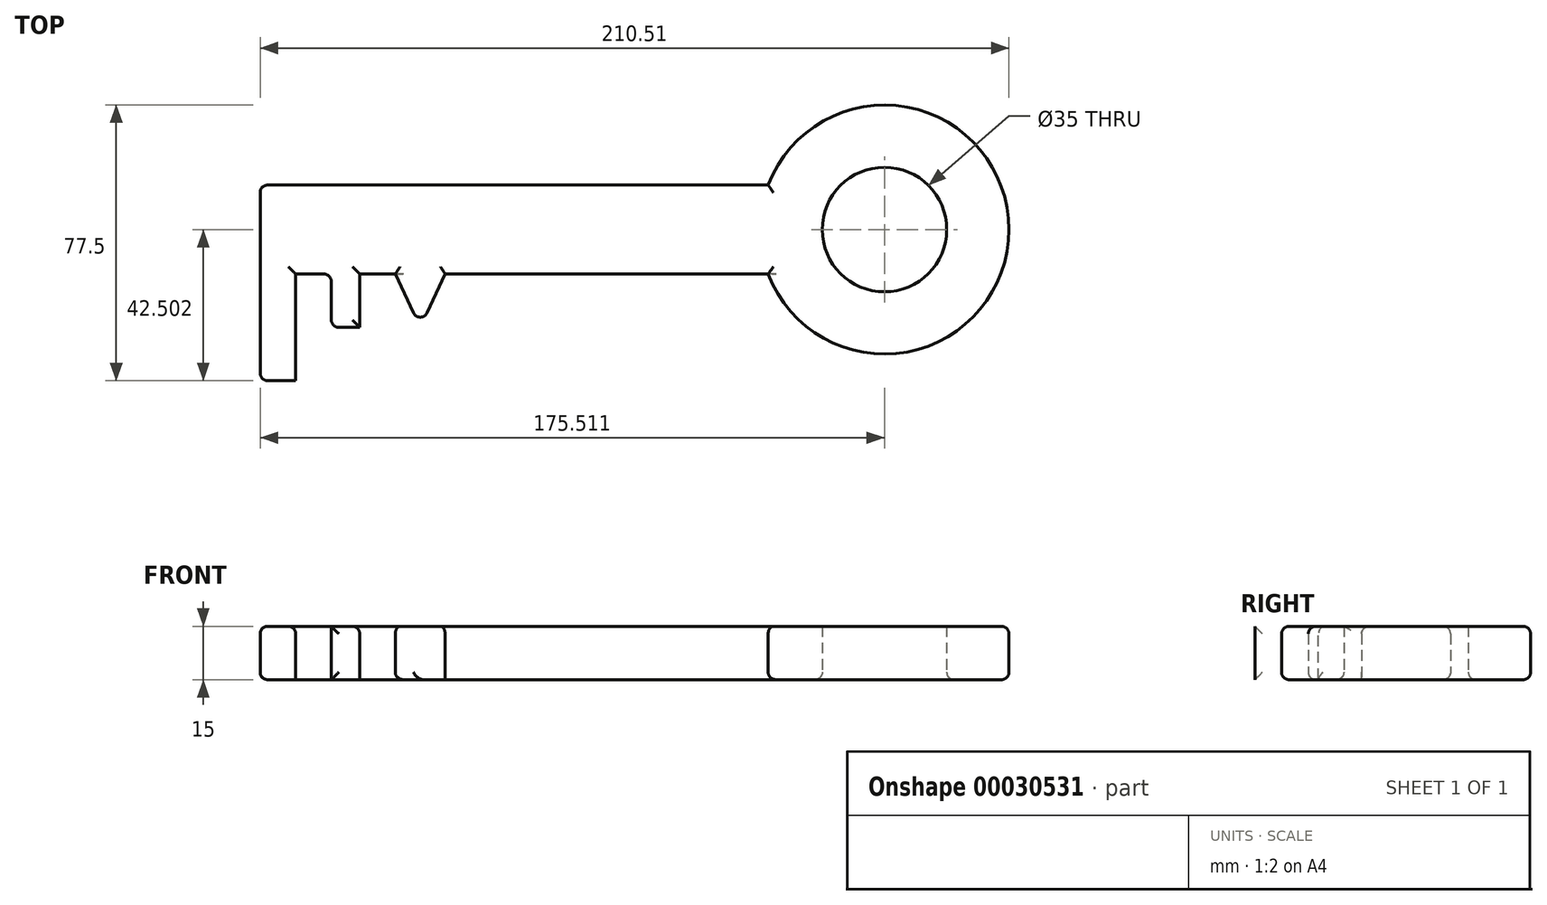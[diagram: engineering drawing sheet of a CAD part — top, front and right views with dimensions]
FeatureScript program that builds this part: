
annotation { "Feature Type Name" : "Feature", "Feature Type Description" : "" }
export const myFeature = defineFeature(function(context is Context, id is Id, definition is map)
    precondition{}
    {
        {
            var Q0;
            Q0=qCreatedBy(makeId("Top.planeOp"),FACE);
            var sketch = newSketch(context, id + "F0", { "sketchPlane" : qUnion([Q0])});
            skLineSegment(sketch, "E0.bottom", {"start": v(-113.6, 29.5) * mm, "end": v(29.23, 29.5) * mm});
            skLineSegment(sketch, "E0.top", {"start": v(-113.6, 4.5) * mm, "end": v(29.23, 4.5) * mm});
            skLineSegment(sketch, "E0.left", {"start": v(-113.6, 29.5) * mm, "end": v(-113.6, 4.5) * mm});
            skLineSegment(sketch, "E0.right", {"start": v(29.23, 29.5) * mm, "end": v(29.23, 4.5) * mm});
            skLineSegment(sketch, "E1.bottom", {"start": v(-113.6, 4.5) * mm, "end": v(-103.6, 4.5) * mm});
            skLineSegment(sketch, "E1.top", {"start": v(-113.6, -25.5) * mm, "end": v(-103.6, -25.5) * mm});
            skLineSegment(sketch, "E1.left", {"start": v(-113.6, 4.5) * mm, "end": v(-113.6, -25.5) * mm});
            skLineSegment(sketch, "E1.right", {"start": v(-103.6, 4.5) * mm, "end": v(-103.6, -25.5) * mm});
            skLineSegment(sketch, "E2.bottom", {"start": v(-93.6, 4.5) * mm, "end": v(-85.6, 4.5) * mm});
            skLineSegment(sketch, "E2.top", {"start": v(-93.6, -10.5) * mm, "end": v(-85.6, -10.5) * mm});
            skLineSegment(sketch, "E2.left", {"start": v(-93.6, 4.5) * mm, "end": v(-93.6, -10.5) * mm});
            skLineSegment(sketch, "E2.right", {"start": v(-85.6, 4.5) * mm, "end": v(-85.6, -10.5) * mm});
            skLineSegment(sketch, "E3", {"start": v(-75.6, 4.5) * mm, "end": v(-68.6, -10.5) * mm});
            skArc(sketch, "E4", {"start": v(29.23, 4.5) * mm, "mid": v(96.92, 17) * mm, "end": v(29.23, 29.5) * mm});
            skCircle(sketch, "E5", {"center": v(61.92, 17) * mm, "radius": 17.5 * mm});
            skLineSegment(sketch, "E6", {"start": v(-61.6, 4.5) * mm, "end": v(-68.6, -10.5) * mm});
            skSolve(sketch);
        }
        {
            var Q0;
            Q0 = qSketchRegion(id + "F0", true);
            extrude(context, id + "F1", {"entities" : qUnion([Q0]), "depth" : 15 * mm});
        }
        {
            var Q0;
            Q0=makeQuery(id+"F1.opExtrude","CAP_EDGE",EDGE,{"disambiguationData":[OSD([sQuery(id+"F0.wireOp",EDGE,"E0.left"),sQuery(id+"F0.wireOp",EDGE,"E1.left")])],"isStart":true});
            var Q1;
            Q1=makeQuery(id+"F1.opExtrude","SWEPT_EDGE",EDGE,{"disambiguationData":[OSD([sQuery(id+"F0.wireOp",EDGE,"E0.bottom"),sQuery(id+"F0.wireOp",EDGE,"E0.left")])]});
            var Q2;
            Q2=makeQuery(id+"F1.opExtrude","CAP_EDGE",EDGE,{"disambiguationData":[OSD([sQuery(id+"F0.wireOp",EDGE,"E0.left"),sQuery(id+"F0.wireOp",EDGE,"E1.left")])],"isStart":false});
            var Q3;
            Q3=makeQuery(id+"F1.opExtrude","SWEPT_EDGE",EDGE,{"disambiguationData":[OSD([sQuery(id+"F0.wireOp",EDGE,"E1.top"),sQuery(id+"F0.wireOp",EDGE,"E1.left")])]});
            var Q4;
            Q4=makeQuery(id+"F1.opExtrude","CAP_EDGE",EDGE,{"disambiguationData":[OSD([sQuery(id+"F0.wireOp",EDGE,"E0.bottom")])],"isStart":true});
            var Q5;
            {var subQ0=sQuery(id+"F0.wireOp",EDGE,"E0.top");Q5=makeQuery(id+"F1.opExtrude","CAP_EDGE",EDGE,{"disambiguationData":[OSD([subQ0]),TDD([makeQuery(id+"F0.imprint","IMPRINT",EDGE,{"disambiguationData":[TD([[makeQuery(id+"F0.imprint","INTERSECT",VERTEX,{"derivedFrom":[subQ0,sQuery(id+"F0.wireOp",EDGE,"E6")]}),-1.0]])],"derivedFrom":subQ0})])],"isStart":false});}
            var Q6;
            Q6=makeQuery(id+"F1.opExtrude","CAP_EDGE",EDGE,{"disambiguationData":[OSD([sQuery(id+"F0.wireOp",EDGE,"E0.bottom")])],"isStart":false});
            var Q7;
            Q7=makeQuery(id+"F1.opExtrude","CAP_EDGE",EDGE,{"disambiguationData":[OSD([sQuery(id+"F0.wireOp",EDGE,"E4")])],"isStart":false});
            var Q8;
            Q8=makeQuery(id+"F1.opExtrude","CAP_EDGE",EDGE,{"disambiguationData":[OSD([sQuery(id+"F0.wireOp",EDGE,"E4")])],"isStart":true});
            var Q9;
            Q9=makeQuery(id+"F1.opExtrude","CAP_EDGE",EDGE,{"disambiguationData":[OSD([sQuery(id+"F0.wireOp",EDGE,"E6")])],"isStart":false});
            var Q10;
            Q10=makeQuery(id+"F1.opExtrude","CAP_EDGE",EDGE,{"disambiguationData":[OSD([sQuery(id+"F0.wireOp",EDGE,"E2.right")])],"isStart":false});
            var Q11;
            {var subQ0=sQuery(id+"F0.wireOp",EDGE,"E0.top");Q11=makeQuery(id+"F1.opExtrude","CAP_EDGE",EDGE,{"disambiguationData":[OSD([subQ0]),TDD([makeQuery(id+"F0.imprint","IMPRINT",EDGE,{"disambiguationData":[TD([[makeQuery(id+"F0.imprint","INTERSECT",VERTEX,{"derivedFrom":[subQ0,sQuery(id+"F0.wireOp",EDGE,"E3")]}),1.0]])],"derivedFrom":subQ0})])],"isStart":false});}
            var Q12;
            Q12=makeQuery(id+"F1.opExtrude","CAP_EDGE",EDGE,{"disambiguationData":[OSD([sQuery(id+"F0.wireOp",EDGE,"E3")])],"isStart":false});
            var Q13;
            Q13=makeQuery(id+"F1.opExtrude","CAP_EDGE",EDGE,{"disambiguationData":[OSD([sQuery(id+"F0.wireOp",EDGE,"E2.top")])],"isStart":false});
            var Q14;
            Q14=makeQuery(id+"F1.opExtrude","SWEPT_EDGE",EDGE,{"disambiguationData":[OSD([sQuery(id+"F0.wireOp",EDGE,"E0.top"),sQuery(id+"F0.wireOp",EDGE,"E2.bottom"),sQuery(id+"F0.wireOp",EDGE,"E2.left")])]});
            var Q15;
            Q15=makeQuery(id+"F1.opExtrude","CAP_EDGE",EDGE,{"disambiguationData":[OSD([sQuery(id+"F0.wireOp",EDGE,"E1.right")])],"isStart":false});
            var Q16;
            Q16=makeQuery(id+"F1.opExtrude","SWEPT_EDGE",EDGE,{"disambiguationData":[OSD([sQuery(id+"F0.wireOp",EDGE,"E2.top"),sQuery(id+"F0.wireOp",EDGE,"E2.left")])]});
            var Q17;
            Q17=makeQuery(id+"F1.opExtrude","CAP_EDGE",EDGE,{"disambiguationData":[OSD([sQuery(id+"F0.wireOp",EDGE,"E2.top")])],"isStart":true});
            var Q18;
            Q18=makeQuery(id+"F1.opExtrude","CAP_EDGE",EDGE,{"disambiguationData":[OSD([sQuery(id+"F0.wireOp",EDGE,"E3")])],"isStart":true});
            var Q19;
            Q19=makeQuery(id+"F1.opExtrude","SWEPT_EDGE",EDGE,{"disambiguationData":[OSD([sQuery(id+"F0.wireOp",EDGE,"E3"),sQuery(id+"F0.wireOp",EDGE,"E6")])]});
            var Q20;
            {var subQ0=sQuery(id+"F0.wireOp",EDGE,"E0.top");Q20=makeQuery(id+"F1.opExtrude","CAP_EDGE",EDGE,{"disambiguationData":[OSD([subQ0]),TDD([makeQuery(id+"F0.imprint","IMPRINT",EDGE,{"disambiguationData":[TD([[makeQuery(id+"F0.imprint","INTERSECT",VERTEX,{"derivedFrom":[subQ0,sQuery(id+"F0.wireOp",EDGE,"E1.bottom"),sQuery(id+"F0.wireOp",EDGE,"E1.right")]}),-1.0]])],"derivedFrom":subQ0})])],"isStart":false});}
            var Q21;
            Q21=makeQuery(id+"F1.opExtrude","CAP_EDGE",EDGE,{"disambiguationData":[OSD([sQuery(id+"F0.wireOp",EDGE,"E5")])],"isStart":true});
            fillet(context, id + "F2", {"entities" : qUnion([Q0, Q1, Q2, Q3, Q4, Q5, Q6, Q7, Q8, Q9, Q10, Q11, Q12, Q13, Q14, Q15, Q16, Q17, Q18, Q19, Q20, Q21]), "radius" : 2.1 * mm, "tangentPropagation" : true, "allowEdgeOverflow" : false});
        }
    });
